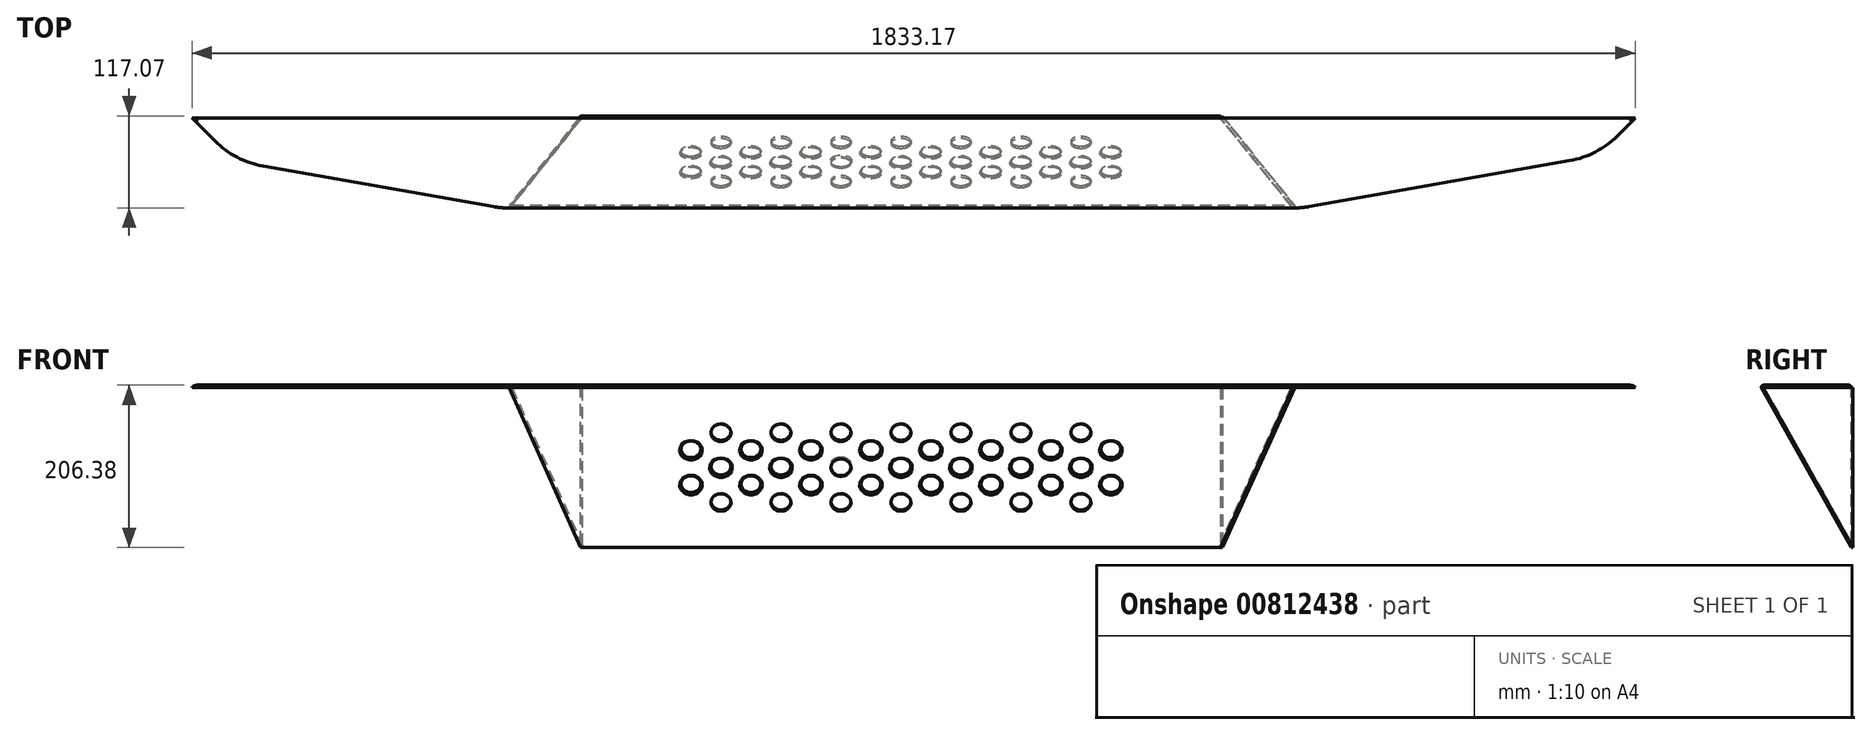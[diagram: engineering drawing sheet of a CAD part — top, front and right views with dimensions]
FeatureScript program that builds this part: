
annotation { "Feature Type Name" : "Feature", "Feature Type Description" : "" }
export const myFeature = defineFeature(function(context is Context, id is Id, definition is map)
    precondition{}
    {
        {
            var Q0;
            Q0=qCreatedBy(makeId("Front.planeOp"),FACE);
            var sketch = newSketch(context, id + "F0", { "sketchPlane" : qUnion([Q0])});
            skLineSegment(sketch, "E0.bottom", {"start": v(-406.77, 0) * mm, "end": v(406.03, 0) * mm, "construction": true});
            skLineSegment(sketch, "E0.top", {"start": v(-406.77, 609.6) * mm, "end": v(406.03, 609.6) * mm, "construction": true});
            skLineSegment(sketch, "E0.left", {"start": v(-406.77, 0) * mm, "end": v(-406.77, 609.6) * mm, "construction": true});
            skLineSegment(sketch, "E0.right", {"start": v(406.03, 0) * mm, "end": v(406.03, 609.6) * mm, "construction": true});
            skLineSegment(sketch, "E1", {"start": v(-952.5, 203.2) * mm, "end": v(952.5, 203.2) * mm});
            skLineSegment(sketch, "E2", {"start": v(0, 0) * mm, "end": v(0, 1021.85) * mm, "construction": true});
            skPoint(sketch, "E3", {"position": v(-406.77, 203.2) * mm});
            skPoint(sketch, "E4", {"position": v(406.03, 203.2) * mm});
            skSolve(sketch);
        }
        {
            var Q0;
            Q0=qCreatedBy(makeId("Top.planeOp"),FACE);
            cPlane(context, id + "F1", {"entities" : qUnion([Q0]), "cplaneType" : CPlaneType.OFFSET, "offset" : 203.2 * mm, "width" : 152.4 * mm, "height" : 152.4 * mm});
        }
        {
            var Q0;
            Q0=qCreatedBy(id+"F1.planeOp",FACE);
            var sketch = newSketch(context, id + "F2", { "sketchPlane" : qUnion([Q0])});
            skLineSegment(sketch, "E5", {"start": v(498, -114.3) * mm, "end": v(-498, -114.3) * mm});
            skPoint(sketch, "E6", {"position": v(0, -114.3) * mm});
            skLineSegment(sketch, "E7", {"start": v(-517.85, -112.56) * mm, "end": v(-810.34, -60.99) * mm});
            skLineSegment(sketch, "E8", {"start": v(-871.31, -29.25) * mm, "end": v(-900.56, 0) * mm});
            skPoint(sketch, "E9.visualSharp", {"position": v(-845.83, -54.73) * mm});
            skArc(sketch, "E9.filletArc", {"start": v(-871.31, -29.25) * mm, "mid": v(-843.27, -49.81) * mm, "end": v(-810.34, -60.99) * mm});
            skPoint(sketch, "E10.visualSharp", {"position": v(-508, -114.3) * mm});
            skArc(sketch, "E10.filletArc", {"start": v(-517.85, -112.56) * mm, "mid": v(-507.96, -113.87) * mm, "end": v(-498, -114.3) * mm});
            skPoint(sketch, "E11.MirrorP", {"position": v(508, -114.3) * mm});
            skPoint(sketch, "E12.MirrorP", {"position": v(845.83, -54.73) * mm});
            skLineSegment(sketch, "E13", {"start": v(517.85, -112.56) * mm, "end": v(849.25, -54.13) * mm});
            skLineSegment(sketch, "E14", {"start": v(910.22, -22.39) * mm, "end": v(932.61, 0) * mm});
            skArc(sketch, "E15.filletArc", {"start": v(498, -114.3) * mm, "mid": v(507.96, -113.87) * mm, "end": v(517.85, -112.56) * mm});
            skPoint(sketch, "E16.visualSharp", {"position": v(884.74, -47.87) * mm});
            skArc(sketch, "E16.filletArc", {"start": v(849.25, -54.13) * mm, "mid": v(882.18, -42.95) * mm, "end": v(910.22, -22.39) * mm});
            skLineSegment(sketch, "E17", {"start": v(932.61, 0) * mm, "end": v(-900.56, 0) * mm});
            skSolve(sketch);
        }
        {
            var Q0;
            Q0=sQuery(id+"F2.wireOp",VERTEX,"E5.end");
            var Q1;
            Q1=sQuery(id+"F0.wireOp",VERTEX,"E3");
            var Q2;
            Q2=sQuery(id+"F0.wireOp",VERTEX,"E0.left.start");
            cPlane(context, id + "F3", {"entities" : qUnion([Q0, Q1, Q2]), "cplaneType" : CPlaneType.THREE_POINT, "offset" : 25.4 * mm, "width" : 152.4 * mm, "height" : 152.4 * mm});
        }
        {
            var Q0;
            Q0=qCreatedBy(id+"F3.planeOp",FACE);
            var sketch = newSketch(context, id + "F4", { "sketchPlane" : qUnion([Q0])});
            skLineSegment(sketch, "E18", {"start": v(-399.99, 203.2) * mm, "end": v(-253.75, 0) * mm});
            skLineSegment(sketch, "E19", {"start": v(-253.75, 0) * mm, "end": v(-253.75, 203.2) * mm});
            skLineSegment(sketch, "E20", {"start": v(-253.75, 203.2) * mm, "end": v(-399.99, 203.2) * mm});
            skPoint(sketch, "E21", {"position": v(-326.87, 101.6) * mm});
            skSolve(sketch);
        }
        {
            var Q0;
            Q0=sQuery(id+"F2.wireOp",VERTEX,"E5.start");
            var Q1;
            Q1=sQuery(id+"F0.wireOp",VERTEX,"E4");
            var Q2;
            Q2=sQuery(id+"F0.wireOp",VERTEX,"E0.right.start");
            cPlane(context, id + "F5", {"entities" : qUnion([Q0, Q1, Q2]), "cplaneType" : CPlaneType.THREE_POINT, "offset" : 25.4 * mm, "width" : 152.4 * mm, "height" : 152.4 * mm});
        }
        {
            var Q0;
            Q0=qCreatedBy(id+"F5.planeOp",FACE);
            var sketch = newSketch(context, id + "F6", { "sketchPlane" : qUnion([Q0])});
            skLineSegment(sketch, "E22", {"start": v(-401.25, 203.2) * mm, "end": v(-254.54, 203.2) * mm});
            skLineSegment(sketch, "E23", {"start": v(-254.54, 203.2) * mm, "end": v(-254.54, 0) * mm});
            skLineSegment(sketch, "E24", {"start": v(-254.54, 0) * mm, "end": v(-401.25, 203.2) * mm});
            skPoint(sketch, "E25", {"position": v(-327.9, 101.6) * mm});
            skSolve(sketch);
        }
        {
            var Q0;
            Q0=sQuery(id+"F6.wireOp",VERTEX,"E22.start");
            var Q1;
            Q1=sQuery(id+"F4.wireOp",VERTEX,"E18.start");
            var Q2;
            Q2=sQuery(id+"F0.wireOp",VERTEX,"E2.start");
            cPlane(context, id + "F7", {"entities" : qUnion([Q0, Q1, Q2]), "cplaneType" : CPlaneType.THREE_POINT, "offset" : 25.4 * mm, "width" : 152.4 * mm, "height" : 152.4 * mm});
        }
        {
            var Q0;
            Q0=qCreatedBy(id+"F7.planeOp",FACE);
            var sketch = newSketch(context, id + "F8", { "sketchPlane" : qUnion([Q0])});
            skLineSegment(sketch, "E26", {"start": v(-452.01, 116.57) * mm, "end": v(452.39, 116.57) * mm, "construction": true});
            skPoint(sketch, "E27", {"position": v(0.19, 116.57) * mm});
            skSolve(sketch);
        }
        {
            var Q0;
            Q0=qCreatedBy(id+"F7.planeOp",FACE);
            var sketch = newSketch(context, id + "F9", { "sketchPlane" : qUnion([Q0])});
            skCircle(sketch, "E28", {"center": v(228.79, 116.57) * mm, "radius": 12.7 * mm});
            skCircle(sketch, "E29.1.0.0", {"center": v(152.59, 116.57) * mm, "radius": 12.7 * mm});
            skCircle(sketch, "E29.2.0.0", {"center": v(76.39, 116.57) * mm, "radius": 12.7 * mm});
            skCircle(sketch, "E29.3.0.0", {"center": v(0.19, 116.57) * mm, "radius": 12.7 * mm});
            skCircle(sketch, "E29.4.0.0", {"center": v(-76.01, 116.57) * mm, "radius": 12.7 * mm});
            skCircle(sketch, "E29.5.0.0", {"center": v(-152.21, 116.57) * mm, "radius": 12.7 * mm});
            skCircle(sketch, "E29.6.0.0", {"center": v(-228.41, 116.57) * mm, "radius": 12.7 * mm});
            skLineSegment(sketch, "E29.direction1", {"start": v(228.79, 116.57) * mm, "end": v(152.59, 116.57) * mm, "construction": true});
            skCircle(sketch, "E30", {"center": v(266.89, 141.97) * mm, "radius": 12.7 * mm});
            skCircle(sketch, "E31.1.0.0", {"center": v(190.69, 141.97) * mm, "radius": 12.7 * mm});
            skCircle(sketch, "E31.2.0.0", {"center": v(114.49, 141.97) * mm, "radius": 12.7 * mm});
            skCircle(sketch, "E31.3.0.0", {"center": v(38.29, 141.97) * mm, "radius": 12.7 * mm});
            skCircle(sketch, "E31.4.0.0", {"center": v(-37.91, 141.97) * mm, "radius": 12.7 * mm});
            skCircle(sketch, "E31.5.0.0", {"center": v(-114.11, 141.97) * mm, "radius": 12.7 * mm});
            skCircle(sketch, "E31.6.0.0", {"center": v(-190.31, 141.97) * mm, "radius": 12.7 * mm});
            skCircle(sketch, "E31.7.0.0", {"center": v(-266.51, 141.97) * mm, "radius": 12.7 * mm});
            skLineSegment(sketch, "E31.direction1", {"start": v(266.89, 141.97) * mm, "end": v(190.69, 141.97) * mm, "construction": true});
            skCircle(sketch, "E32", {"center": v(266.89, 91.17) * mm, "radius": 12.7 * mm});
            skCircle(sketch, "E33.1.0.0", {"center": v(190.69, 91.17) * mm, "radius": 12.7 * mm});
            skCircle(sketch, "E33.2.0.0", {"center": v(114.49, 91.17) * mm, "radius": 12.7 * mm});
            skCircle(sketch, "E33.3.0.0", {"center": v(38.29, 91.17) * mm, "radius": 12.7 * mm});
            skCircle(sketch, "E33.4.0.0", {"center": v(-37.91, 91.17) * mm, "radius": 12.7 * mm});
            skCircle(sketch, "E33.5.0.0", {"center": v(-114.11, 91.17) * mm, "radius": 12.7 * mm});
            skCircle(sketch, "E33.6.0.0", {"center": v(-190.31, 91.17) * mm, "radius": 12.7 * mm});
            skCircle(sketch, "E33.7.0.0", {"center": v(-266.51, 91.17) * mm, "radius": 12.7 * mm});
            skLineSegment(sketch, "E33.direction1", {"start": v(266.89, 91.17) * mm, "end": v(190.69, 91.17) * mm, "construction": true});
            skLineSegment(sketch, "E34", {"start": v(406.77, 0) * mm, "end": v(-406.03, 0) * mm});
            skLineSegment(sketch, "E35", {"start": v(406.77, 0) * mm, "end": v(498, 233.14) * mm});
            skLineSegment(sketch, "E36", {"start": v(498, 233.14) * mm, "end": v(-498, 233.14) * mm});
            skLineSegment(sketch, "E37", {"start": v(-498, 233.14) * mm, "end": v(-406.03, 0) * mm});
            skCircle(sketch, "E38", {"center": v(228.79, 167.37) * mm, "radius": 12.7 * mm});
            skPoint(sketch, "E38.centerSnap0", {"position": v(228.79, 141.97) * mm});
            skCircle(sketch, "E39", {"center": v(228.79, 65.77) * mm, "radius": 12.7 * mm});
            skCircle(sketch, "E40.1.0.0", {"center": v(152.59, 167.37) * mm, "radius": 12.7 * mm});
            skCircle(sketch, "E40.1.0.1", {"center": v(152.59, 65.77) * mm, "radius": 12.7 * mm});
            skCircle(sketch, "E40.2.0.0", {"center": v(76.39, 167.37) * mm, "radius": 12.7 * mm});
            skCircle(sketch, "E40.2.0.1", {"center": v(76.39, 65.77) * mm, "radius": 12.7 * mm});
            skCircle(sketch, "E40.3.0.0", {"center": v(0.19, 167.37) * mm, "radius": 12.7 * mm});
            skCircle(sketch, "E40.3.0.1", {"center": v(0.19, 65.77) * mm, "radius": 12.7 * mm});
            skCircle(sketch, "E40.4.0.0", {"center": v(-76.01, 167.37) * mm, "radius": 12.7 * mm});
            skCircle(sketch, "E40.4.0.1", {"center": v(-76.01, 65.77) * mm, "radius": 12.7 * mm});
            skCircle(sketch, "E40.5.0.0", {"center": v(-152.21, 167.37) * mm, "radius": 12.7 * mm});
            skCircle(sketch, "E40.5.0.1", {"center": v(-152.21, 65.77) * mm, "radius": 12.7 * mm});
            skCircle(sketch, "E40.6.0.0", {"center": v(-228.41, 167.37) * mm, "radius": 12.7 * mm});
            skCircle(sketch, "E40.6.0.1", {"center": v(-228.41, 65.77) * mm, "radius": 12.7 * mm});
            skLineSegment(sketch, "E40.direction1", {"start": v(228.79, 167.37) * mm, "end": v(152.59, 167.37) * mm, "construction": true});
            skSolve(sketch);
        }
        {
            var Q0;
            Q0=makeQuery(id+"F9.imprint","IMPRINT",FACE,{"disambiguationData":[TD([[makeQuery(id+"F9.imprint","IMPRINT",EDGE,{"derivedFrom":sQuery(id+"F9.wireOp",EDGE,"E28")}),-1.0]])]});
            extrude(context, id + "F10", {"entities" : qUnion([Q0]), "depth" : 3.17 * mm, "offsetDistance" : 25.4 * mm});
        }
        {
            var Q0;
            Q0=makeQuery(id+"F10.opExtrude","CAP_EDGE",EDGE,{"disambiguationData":[OSD([sQuery(id+"F9.wireOp",EDGE,"E33.5.0.0")])],"isStart":true});
            var Q1;
            Q1=makeQuery(id+"F10.opExtrude","CAP_EDGE",EDGE,{"disambiguationData":[OSD([sQuery(id+"F9.wireOp",EDGE,"E30")])],"isStart":true});
            var Q2;
            Q2=makeQuery(id+"F10.opExtrude","CAP_EDGE",EDGE,{"disambiguationData":[OSD([sQuery(id+"F9.wireOp",EDGE,"E31.1.0.0")])],"isStart":true});
            var Q3;
            Q3=makeQuery(id+"F10.opExtrude","CAP_EDGE",EDGE,{"disambiguationData":[OSD([sQuery(id+"F9.wireOp",EDGE,"E28")])],"isStart":true});
            var Q4;
            Q4=makeQuery(id+"F10.opExtrude","CAP_EDGE",EDGE,{"disambiguationData":[OSD([sQuery(id+"F9.wireOp",EDGE,"E32")])],"isStart":true});
            var Q5;
            Q5=makeQuery(id+"F10.opExtrude","CAP_EDGE",EDGE,{"disambiguationData":[OSD([sQuery(id+"F9.wireOp",EDGE,"E33.1.0.0")])],"isStart":true});
            var Q6;
            Q6=makeQuery(id+"F10.opExtrude","CAP_EDGE",EDGE,{"disambiguationData":[OSD([sQuery(id+"F9.wireOp",EDGE,"E29.1.0.0")])],"isStart":true});
            var Q7;
            Q7=makeQuery(id+"F10.opExtrude","CAP_EDGE",EDGE,{"disambiguationData":[OSD([sQuery(id+"F9.wireOp",EDGE,"E31.2.0.0")])],"isStart":true});
            var Q8;
            Q8=makeQuery(id+"F10.opExtrude","CAP_EDGE",EDGE,{"disambiguationData":[OSD([sQuery(id+"F9.wireOp",EDGE,"E33.2.0.0")])],"isStart":true});
            var Q9;
            Q9=makeQuery(id+"F10.opExtrude","CAP_EDGE",EDGE,{"disambiguationData":[OSD([sQuery(id+"F9.wireOp",EDGE,"E29.2.0.0")])],"isStart":false});
            var Q10;
            Q10=makeQuery(id+"F10.opExtrude","CAP_EDGE",EDGE,{"disambiguationData":[OSD([sQuery(id+"F9.wireOp",EDGE,"E31.3.0.0")])],"isStart":true});
            var Q11;
            Q11=makeQuery(id+"F10.opExtrude","CAP_EDGE",EDGE,{"disambiguationData":[OSD([sQuery(id+"F9.wireOp",EDGE,"E33.3.0.0")])],"isStart":true});
            var Q12;
            Q12=makeQuery(id+"F10.opExtrude","CAP_EDGE",EDGE,{"disambiguationData":[OSD([sQuery(id+"F9.wireOp",EDGE,"E29.3.0.0")])],"isStart":true});
            var Q13;
            Q13=makeQuery(id+"F10.opExtrude","CAP_EDGE",EDGE,{"disambiguationData":[OSD([sQuery(id+"F9.wireOp",EDGE,"E31.4.0.0")])],"isStart":true});
            var Q14;
            Q14=makeQuery(id+"F10.opExtrude","CAP_EDGE",EDGE,{"disambiguationData":[OSD([sQuery(id+"F9.wireOp",EDGE,"E33.4.0.0")])],"isStart":true});
            var Q15;
            Q15=makeQuery(id+"F10.opExtrude","CAP_EDGE",EDGE,{"disambiguationData":[OSD([sQuery(id+"F9.wireOp",EDGE,"E29.4.0.0")])],"isStart":true});
            var Q16;
            Q16=makeQuery(id+"F10.opExtrude","CAP_EDGE",EDGE,{"disambiguationData":[OSD([sQuery(id+"F9.wireOp",EDGE,"E31.5.0.0")])],"isStart":true});
            var Q17;
            Q17=makeQuery(id+"F10.opExtrude","CAP_EDGE",EDGE,{"disambiguationData":[OSD([sQuery(id+"F9.wireOp",EDGE,"E29.5.0.0")])],"isStart":true});
            var Q18;
            Q18=makeQuery(id+"F10.opExtrude","CAP_EDGE",EDGE,{"disambiguationData":[OSD([sQuery(id+"F9.wireOp",EDGE,"E31.6.0.0")])],"isStart":true});
            var Q19;
            Q19=makeQuery(id+"F10.opExtrude","CAP_EDGE",EDGE,{"disambiguationData":[OSD([sQuery(id+"F9.wireOp",EDGE,"E31.7.0.0")])],"isStart":true});
            var Q20;
            Q20=makeQuery(id+"F10.opExtrude","CAP_EDGE",EDGE,{"disambiguationData":[OSD([sQuery(id+"F9.wireOp",EDGE,"E29.6.0.0")])],"isStart":true});
            var Q21;
            Q21=makeQuery(id+"F10.opExtrude","CAP_EDGE",EDGE,{"disambiguationData":[OSD([sQuery(id+"F9.wireOp",EDGE,"E33.6.0.0")])],"isStart":true});
            var Q22;
            Q22=makeQuery(id+"F10.opExtrude","CAP_EDGE",EDGE,{"disambiguationData":[OSD([sQuery(id+"F9.wireOp",EDGE,"E33.7.0.0")])],"isStart":true});
            chamfer(context, id + "F11", {"entities" : qUnion([Q0, Q1, Q2, Q3, Q4, Q5, Q6, Q7, Q8, Q9, Q10, Q11, Q12, Q13, Q14, Q15, Q16, Q17, Q18, Q19, Q20, Q21, Q22]), "width" : 1.52 * mm, "tangentPropagation" : true});
        }
        {
            var Q0;
            Q0=makeQuery(id+"F2.imprint","IMPRINT",FACE,{"disambiguationData":[TD([[makeQuery(id+"F2.imprint","IMPRINT",EDGE,{"derivedFrom":sQuery(id+"F2.wireOp",EDGE,"E5")}),-1.0]])]});
            extrude(context, id + "F12", {"entities" : qUnion([Q0]), "operationType" : NewBodyOperationType.ADD, "depth" : 3.17 * mm, "offsetDistance" : 25.4 * mm});
        }
        {
            var Q0;
            Q0=makeQuery(id+"F12.opExtrude","CAP_FACE",FACE,{"disambiguationData":[OSD([sQuery(id+"F2.wireOp",EDGE,"E5"),sQuery(id+"F2.wireOp",EDGE,"E7"),sQuery(id+"F2.wireOp",EDGE,"E8"),sQuery(id+"F2.wireOp",EDGE,"E9.filletArc"),sQuery(id+"F2.wireOp",EDGE,"E10.filletArc"),sQuery(id+"F2.wireOp",EDGE,"E13"),sQuery(id+"F2.wireOp",EDGE,"E14"),sQuery(id+"F2.wireOp",EDGE,"E15.filletArc"),sQuery(id+"F2.wireOp",EDGE,"E16.filletArc"),sQuery(id+"F2.wireOp",EDGE,"E17")])],"isStart":false});
            fillet(context, id + "F13", {"entities" : qUnion([Q0]), "radius" : 3.17 * mm, "tangentPropagation" : true, "allowEdgeOverflow" : false});
        }
        {
            var Q0;
            Q0=makeQuery(id+"F6.imprint","IMPRINT",FACE,{"disambiguationData":[TD([[makeQuery(id+"F6.imprint","IMPRINT",EDGE,{"derivedFrom":sQuery(id+"F6.wireOp",EDGE,"E22")}),-1.0]])]});
            var Q1;
            Q1=makeQuery(id+"F4.imprint","IMPRINT",FACE,{"disambiguationData":[TD([[makeQuery(id+"F4.imprint","IMPRINT",EDGE,{"derivedFrom":sQuery(id+"F4.wireOp",EDGE,"E18")}),1.0]])]});
            extrude(context, id + "F14", {"entities" : qUnion([Q0, Q1]), "operationType" : NewBodyOperationType.ADD, "depth" : 3.17 * mm, "offsetDistance" : 25.4 * mm});
        }
    });
